# Revit family: laser_blade_xs_wall_washer_q599
name_source: partatom
category: Lighting Fixtures
units: mm (PartAtom-declared; Revit-internal decimal feet)

## family parameters
Cut with Voids When Loaded = No
Host = Face
Light Source = No
Part Type = Normal
Room Calculation Point = No
Round Connector Dimension = Use Diameter
Shared = No

## types (1)
- Laser Blade XS Wall Washer (1 x LED, 530 lm, 4000K)
    Apparent Load = 6 VA
    CIE Flux Codes = 60 86 98 100 33
    Color Rendering = 90
    Color Temperature = 4000K
    Default Elevation = 1800 mm
    Description = Q599 : 
Miniaturized recessed linear luminaire for LED lamps. Despite the ultracompact size of the product, the patented technology of the optic system guarantees an efficient and homogeneous effect on walls from top to bottom and avoids shadow zones near the ceiling. Main body with die-cast zamak radiant surface, minimal (frameless) version for mounting flush with the ceiling. Flux enhancer - superpure aluminium reflector - asymmetrical textured PMMA screen - black polycarbonate internal perimeter frame. Ballast not included, available with separate code.


Q599.04 - Minimal 3 LED section - Wall Washer - 5.8W 530lm - 4000K - CRI 90 - Black
A23W - Lamp LED Neutral White CRI>90
    Height = 0 mm  [stored 0 ft]
    Lamp = 1 x LED
    Lamp Light Flux = 530 lm
    Lamp count = 1
    Length = 54 mm
    Lifetime = 70000 h
    Luminous efficacy = 30 lm/W
    Manufacturer = iGuzzini
    ModVariant = No
    Model = Q599
    Mounting Place = Ceiling
    Mounting Type = Recessed
    Number of Poles = 1
    OnlyDefault = Yes
    Power Factor = 1
    Product Name = Laser Blade XS Wall Washer
    Product group = recessed luminaire
    ProductGroupID = 4
    Protection Class = Protection class
    Protection Degree = Degree of protection
    RLX_Detail_Level = 1
    RLX_Emergency_Light_Flux = 0 lm
    RLX_Emergency_Type = 0
    RLX_Emergency_Type_DB = No
    RlxData = <blob elided: 17717 chars, md5=18098d5e>
    Socket = socket
    Standby Power = 0 W
    System Light Flux = 175 lm
    System Power = 6 W
    Type Comments = Product without accessories
    Type Image = 03_laserblade_s_ww_q584_min_img0008605_thum.jpg
    URL = http://relux.com
    VarID = ---
    Voltage = 0 V
    Weight = 0.00 kg
    Width = 22 mm

note: [stored X ft] marks values corroborated as IEEE doubles in the binary element streams (Revit-internal decimal feet)

## geometry (parser evidence)
native form markers: Blend x4, Sweep x13
no freeform markers — native parametric forms only
